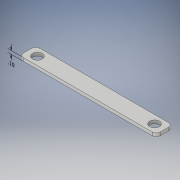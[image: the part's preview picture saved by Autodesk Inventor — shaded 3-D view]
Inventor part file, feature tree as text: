
AUTODESK INVENTOR PART (.ipt)
format: ipt  version: 2018 (Build 220112000, 112)  size: 126,464 bytes
history: native  units: in
note: dims shown in document units (in); Inventor stores cm internally (conversion verified against a paired STEP export)
features: sketch x3, other x2, extrude x2, fillet x1, hole x1
ambient origin geometry x8: Origin, YZ Plane, XZ Plane, XY Plane, X Axis, Y Axis, Z Axis, Center Point
bodies: Solid1 (feature_tree)
feature tree (9):
  other  "Annotations"
  extrude  "Extrusion1"  Depth=0.5in
  fillet  "Fillet1"  Radius=0.1in
  extrude  "Extrusion2"  Depth=0.125in
  hole  "Hole1"  [1 undecoded]
  sketch  "Sketch1"  dims[d0=4.2in d1=0.5in d2=0.1in d3=0.0in]
  sketch  "Sketch2"  dims[d4=0.125in d5=0.3in]
  sketch  "Sketch3"  dims[d6=0.3in d7=0.3in d8=0.3in d9=0.1in d10=0.0in d11=0.3in d12=0.3in d13=0.3in d14=0.75in d15=0.375in d16=0.25in d17=0.5635in d18=1.0in d19=0.8108in d20=0.0931in d21=0.0926in d22=0.1in]
  other  "Linear Dimension 1"
note: 1 required parameter value undecoded (feature->parameter linkage not recoverable at this tier; creation-order binding heuristic only, values carry confidence <= 0.55)
